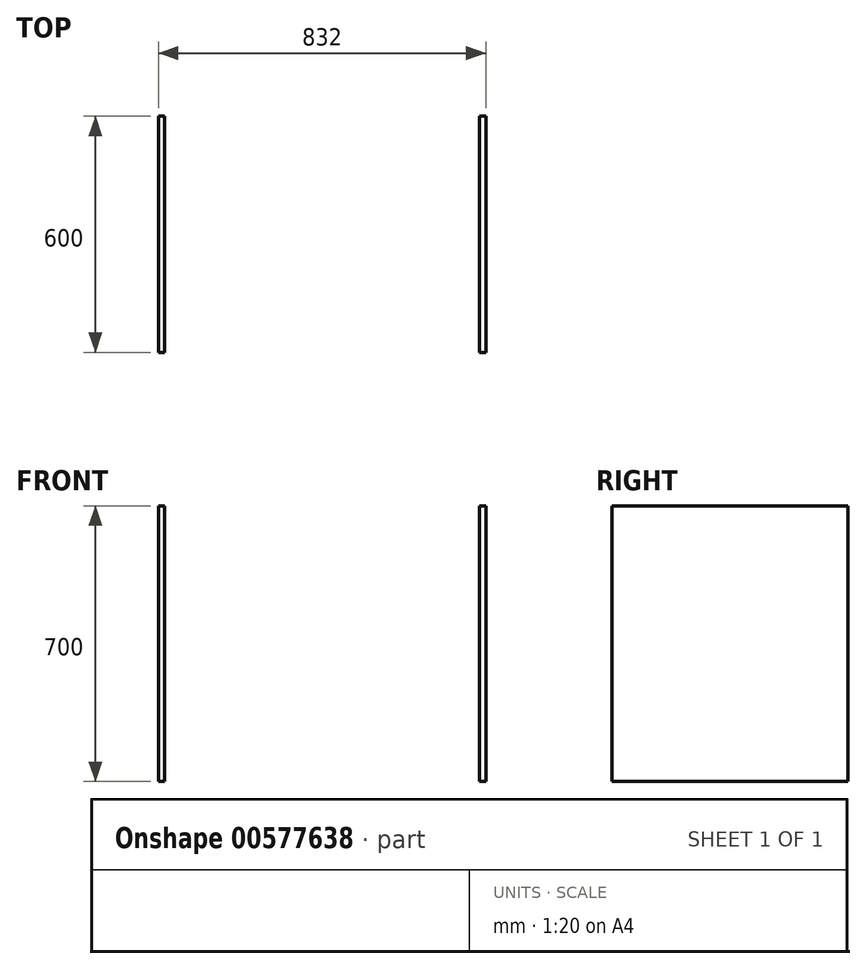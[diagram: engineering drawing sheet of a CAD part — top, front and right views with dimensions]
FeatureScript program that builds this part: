
annotation { "Feature Type Name" : "Feature", "Feature Type Description" : "" }
export const myFeature = defineFeature(function(context is Context, id is Id, definition is map)
    precondition{}
    {
        {
            assignVariable(context, id + "F0", {"name" : "Gas_Path", "anyValue" : 800});
        }
        {
            var Q0;
            Q0=qCreatedBy(makeId("Right.planeOp"),FACE);
            var sketch = newSketch(context, id + "F1", { "sketchPlane" : qUnion([Q0])});
            skCircle(sketch, "E0", {"center": v(0, 0) * mm, "radius": 3 * mm});
            skSolve(sketch);
        }
        {
            var Q0;
            Q0=qCreatedBy(makeId("Right.planeOp"),FACE);
            cPlane(context, id + "F2", {"entities" : qUnion([Q0]), "cplaneType" : CPlaneType.OFFSET, "offset" : (getVariable(context, 'Gas_Path') / 2) * mm, "oppositeDirection" : true, "width" : 150 * mm, "height" : 150 * mm});
        }
        {
            var Q0;
            Q0=qCreatedBy(id+"F2.planeOp",FACE);
            var sketch = newSketch(context, id + "F3", { "sketchPlane" : qUnion([Q0])});
            skPoint(sketch, "E1.0", {"position": v(0, 0) * mm});
            skLineSegment(sketch, "E2.bottom", {"start": v(100, 200) * mm, "end": v(-500, 200) * mm});
            skLineSegment(sketch, "E2.top", {"start": v(100, -500) * mm, "end": v(-500, -500) * mm});
            skLineSegment(sketch, "E2.left", {"start": v(100, 200) * mm, "end": v(100, -500) * mm});
            skLineSegment(sketch, "E2.right", {"start": v(-500, 200) * mm, "end": v(-500, -500) * mm});
            skSolve(sketch);
        }
        {
            var Q0;
            Q0=makeQuery(id+"F3.imprint","IMPRINT",FACE,{"disambiguationData":[TD([[makeQuery(id+"F3.imprint","IMPRINT",EDGE,{"derivedFrom":sQuery(id+"F3.wireOp",EDGE,"E2.bottom")}),1.0]])]});
            extrude(context, id + "F4", {"entities" : qUnion([Q0]), "oppositeDirection" : true, "depth" : 16 * mm, "offsetDistance" : 25 * mm});
        }
        {
            var Q0;
            Q0=makeQuery(id+"F4.opExtrude","SWEPT_BODY",BODY,{"disambiguationData":[OSD([sQuery(id+"F3.wireOp",EDGE,"E2.bottom"),sQuery(id+"F3.wireOp",EDGE,"E2.top"),sQuery(id+"F3.wireOp",EDGE,"E2.left"),sQuery(id+"F3.wireOp",EDGE,"E2.right")])]});
            var Q1;
            Q1=qCreatedBy(makeId("Right.planeOp"),FACE);
            mirror(context, id + "F5", {"entities" : qUnion([Q0]), "mirrorPlane" : qUnion([Q1])});
        }
    });
